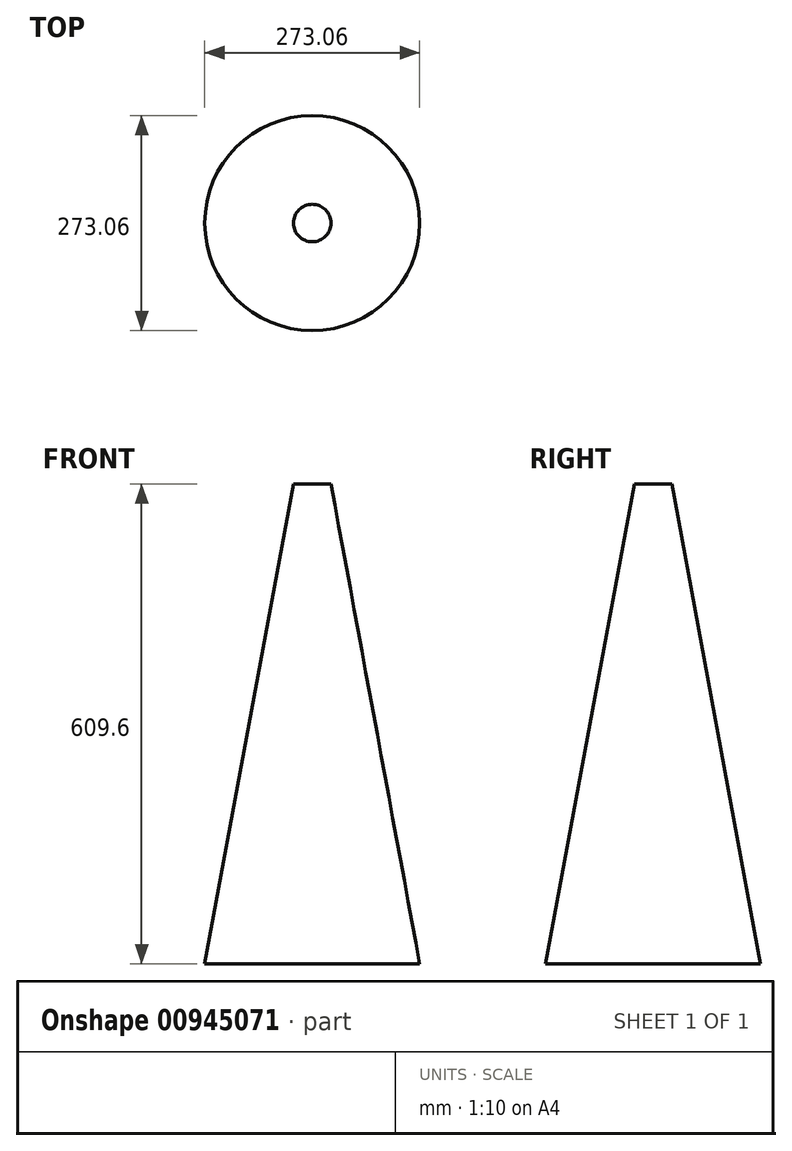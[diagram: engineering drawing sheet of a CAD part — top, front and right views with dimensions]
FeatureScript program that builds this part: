
annotation { "Feature Type Name" : "Feature", "Feature Type Description" : "" }
export const myFeature = defineFeature(function(context is Context, id is Id, definition is map)
    precondition{}
    {
        {
            var Q0;
            Q0=qCreatedBy(makeId("Top.planeOp"),FACE);
            var sketch = newSketch(context, id + "F0", { "sketchPlane" : qUnion([Q0])});
            skCircle(sketch, "E0", {"center": v(0, 0) * mm, "radius": 23.81 * mm});
            skSolve(sketch);
        }
        {
            var Q0;
            Q0=qCreatedBy(makeId("Top.planeOp"),FACE);
            cPlane(context, id + "F1", {"entities" : qUnion([Q0]), "cplaneType" : CPlaneType.OFFSET, "offset" : 609.6 * mm, "oppositeDirection" : true, "width" : 152.4 * mm, "height" : 152.4 * mm});
        }
        {
            var Q0;
            Q0=qCreatedBy(id+"F1.planeOp",FACE);
            var sketch = newSketch(context, id + "F2", { "sketchPlane" : qUnion([Q0])});
            skCircle(sketch, "E1", {"center": v(0, 0) * mm, "radius": 136.53 * mm});
            skSolve(sketch);
        }
        {
            var Q0;
            Q0=makeQuery(id+"F0.imprint","IMPRINT",FACE,{"disambiguationData":[TD([[makeQuery(id+"F0.imprint","IMPRINT",EDGE,{"derivedFrom":sQuery(id+"F0.wireOp",EDGE,"E0")}),1.0]])]});
            var Q1;
            Q1=makeQuery(id+"F2.imprint","IMPRINT",FACE,{"disambiguationData":[TD([[makeQuery(id+"F2.imprint","IMPRINT",EDGE,{"derivedFrom":sQuery(id+"F2.wireOp",EDGE,"E1")}),1.0]])]});
            loft(context, id + "F3", {"sheetProfilesArray" : [{ "sheetProfileEntities" : qUnion([Q0]) }, { "sheetProfileEntities" : qUnion([Q1]) }]});
        }
    });
